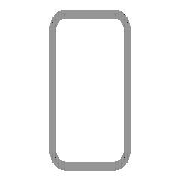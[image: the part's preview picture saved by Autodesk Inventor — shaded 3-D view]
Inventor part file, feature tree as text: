
AUTODESK INVENTOR PART (.ipt)
format: ipt  version: 2025 (Build 290162010, 162A)  size: 135,168 bytes
history: native  units: mm (DEFAULTED — no unit token found)
features: other x4, sketch x1, plane x1
ambient origin geometry x8: Origin, YZ Plane, XZ Plane, XY Plane, X Axis, Y Axis, Z Axis, Center Point
bodies: Solid1 (feature_tree), Body (feature_tree)
feature tree (6):
  parser-record x1  (decoder bookkeeping rows leaked as tree rows — omitted from the tree; the rows remain in map.json)
  other  "Driven Length"
  other  "Start Plane"
  other  "End Plane"
  sketch  "Sketch3"  dims[d3=1290.0mm d4=0.0mm d7=6.0mm d9=40.0mm d11=60.0mm d12=3.0mm d13=40.0mm d14=1330.0mm d15=20.0mm d16=30.0mm d17=90.0deg d18=1290.0mm]
  plane  "Work Plane3"
